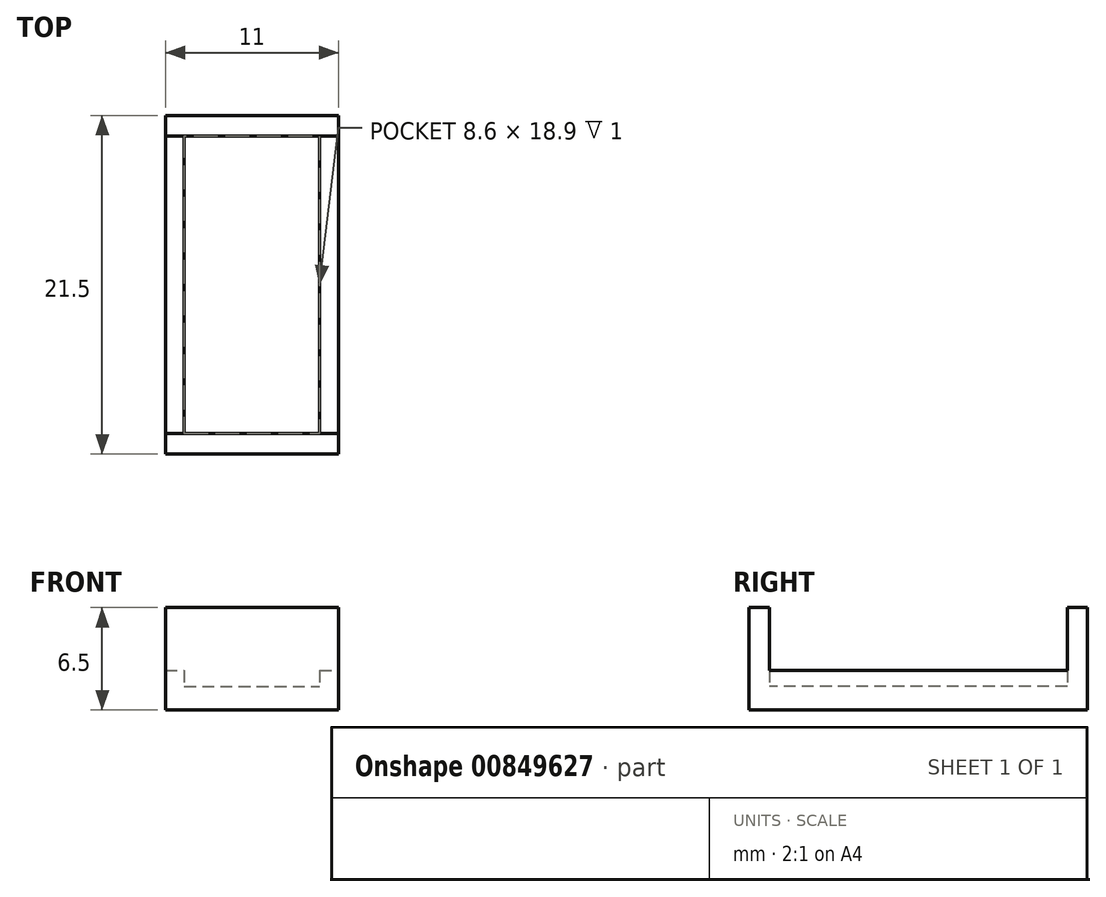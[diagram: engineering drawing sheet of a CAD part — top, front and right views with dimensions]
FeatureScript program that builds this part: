
annotation { "Feature Type Name" : "Feature", "Feature Type Description" : "" }
export const myFeature = defineFeature(function(context is Context, id is Id, definition is map)
    precondition{}
    {
        {
            var Q0;
            Q0=qCreatedBy(makeId("Top.planeOp"),FACE);
            var sketch = newSketch(context, id + "F0", { "sketchPlane" : qUnion([Q0])});
            skLineSegment(sketch, "E0.bottom", {"start": v(5.5, -10.75) * mm, "end": v(-5.5, -10.75) * mm});
            skLineSegment(sketch, "E0.top", {"start": v(5.5, 10.75) * mm, "end": v(-5.5, 10.75) * mm});
            skLineSegment(sketch, "E0.left", {"start": v(5.5, -10.75) * mm, "end": v(5.5, 10.75) * mm});
            skLineSegment(sketch, "E0.right", {"start": v(-5.5, -10.75) * mm, "end": v(-5.5, 10.75) * mm});
            skPoint(sketch, "E0.middle", {"position": v(0, 0) * mm});
            skSolve(sketch);
        }
        {
            var Q0;
            Q0=makeQuery(id+"F0.imprint","IMPRINT",FACE,{"disambiguationData":[TD([[makeQuery(id+"F0.imprint","IMPRINT",EDGE,{"derivedFrom":sQuery(id+"F0.wireOp",EDGE,"E0.bottom")}),-1.0]])]});
            extrude(context, id + "F1", {"entities" : qUnion([Q0]), "depth" : 6.5 * mm, "offsetDistance" : 25 * mm});
        }
        {
            var Q0;
            Q0=makeQuery(id+"F1.opExtrude","CAP_FACE",FACE,{"disambiguationData":[OSD([sQuery(id+"F0.wireOp",EDGE,"E0.bottom"),sQuery(id+"F0.wireOp",EDGE,"E0.top"),sQuery(id+"F0.wireOp",EDGE,"E0.left"),sQuery(id+"F0.wireOp",EDGE,"E0.right")])],"isStart":false});
            var sketch = newSketch(context, id + "F2", { "sketchPlane" : qUnion([Q0])});
            skLineSegment(sketch, "E1.bottom", {"start": v(-6.25, -9.45) * mm, "end": v(6.25, -9.45) * mm});
            skLineSegment(sketch, "E1.top", {"start": v(-6.25, 9.45) * mm, "end": v(6.25, 9.45) * mm});
            skLineSegment(sketch, "E1.left", {"start": v(-6.25, -9.45) * mm, "end": v(-6.25, 9.45) * mm});
            skLineSegment(sketch, "E1.right", {"start": v(6.25, -9.45) * mm, "end": v(6.25, 9.45) * mm});
            skPoint(sketch, "E1.middle", {"position": v(0, 0) * mm});
            skSolve(sketch);
        }
        {
            var Q0;
            Q0=makeQuery(id+"F2.imprint","IMPRINT",FACE,{"disambiguationData":[TD([[makeQuery(id+"F2.imprint","IMPRINT",EDGE,{"derivedFrom":sQuery(id+"F2.wireOp",EDGE,"E1.bottom")}),1.0]])]});
            extrude(context, id + "F3", {"entities" : qUnion([Q0]), "operationType" : NewBodyOperationType.REMOVE, "oppositeDirection" : true, "depth" : 5 * mm, "offsetDistance" : 25 * mm});
        }
        {
            var Q0;
            Q0=makeQuery(id+"F3.boolean.opBoolean","COPY",FACE,{"derivedFrom":makeQuery(id+"F3.opExtrude","CAP_FACE",FACE,{"disambiguationData":[OSD([sQuery(id+"F2.wireOp",EDGE,"E1.bottom"),sQuery(id+"F2.wireOp",EDGE,"E1.top"),sQuery(id+"F2.wireOp",EDGE,"E1.left"),sQuery(id+"F2.wireOp",EDGE,"E1.right")])],"isStart":false})});
            var Q1;
            Q1=makeQuery(id+"F3.boolean.opBoolean","COPY",FACE,{"derivedFrom":makeQuery(id+"F3.opExtrude","CAP_FACE",FACE,{"disambiguationData":[OSD([sQuery(id+"F2.wireOp",EDGE,"E1.bottom"),sQuery(id+"F2.wireOp",EDGE,"E1.top"),sQuery(id+"F2.wireOp",EDGE,"E1.left"),sQuery(id+"F2.wireOp",EDGE,"E1.right")])],"isStart":false})});
            var Q2;
            {var subQ0=sQuery(id+"F0.wireOp",EDGE,"E0.top");var subQ1=sQuery(id+"F0.wireOp",EDGE,"E0.left");var subQ2=sQuery(id+"F0.wireOp",EDGE,"E0.right");Q2=makeQuery(id+"F3.boolean.opBoolean","SPLIT",FACE,{"disambiguationData":[TD([makeQuery(id+"F1.opExtrude","SWEPT_FACE",FACE,{"disambiguationData":[OSD([subQ0])]})])],"derivedFrom":makeQuery(id+"F1.opExtrude","CAP_FACE",FACE,{"disambiguationData":[OSD([sQuery(id+"F0.wireOp",EDGE,"E0.bottom"),subQ0,subQ1,subQ2])],"isStart":false})});}
            var sketch = newSketch(context, id + "F4", { "sketchPlane" : qUnion([Q0, Q1, Q2])});
            skLineSegment(sketch, "E2.bottom", {"start": v(-5.5, 9.45) * mm, "end": v(-4.3, 9.45) * mm});
            skLineSegment(sketch, "E2.top", {"start": v(-5.5, -9.45) * mm, "end": v(-4.3, -9.45) * mm});
            skLineSegment(sketch, "E2.left", {"start": v(-5.5, 9.45) * mm, "end": v(-5.5, -9.45) * mm});
            skLineSegment(sketch, "E2.right", {"start": v(-4.3, 9.45) * mm, "end": v(-4.3, -9.45) * mm});
            skLineSegment(sketch, "E3.bottom", {"start": v(4.3, 9.45) * mm, "end": v(5.5, 9.45) * mm});
            skLineSegment(sketch, "E3.top", {"start": v(4.3, -9.45) * mm, "end": v(5.5, -9.45) * mm});
            skLineSegment(sketch, "E3.left", {"start": v(4.3, 9.45) * mm, "end": v(4.3, -9.45) * mm});
            skLineSegment(sketch, "E3.right", {"start": v(5.5, 9.45) * mm, "end": v(5.5, -9.45) * mm});
            skSolve(sketch);
        }
        {
            var Q0;
            Q0=makeQuery(id+"F4.imprint","IMPRINT",FACE,{"disambiguationData":[TD([[makeQuery(id+"F4.imprint","IMPRINT",EDGE,{"derivedFrom":sQuery(id+"F4.wireOp",EDGE,"E2.bottom")}),-1.0]])]});
            var Q1;
            Q1=makeQuery(id+"F4.imprint","IMPRINT",FACE,{"disambiguationData":[TD([[makeQuery(id+"F4.imprint","IMPRINT",EDGE,{"derivedFrom":sQuery(id+"F4.wireOp",EDGE,"E3.bottom")}),-1.0]])]});
            extrude(context, id + "F5", {"entities" : qUnion([Q0, Q1]), "operationType" : NewBodyOperationType.ADD, "depth" : 1 * mm, "offsetDistance" : 25 * mm});
        }
    });
